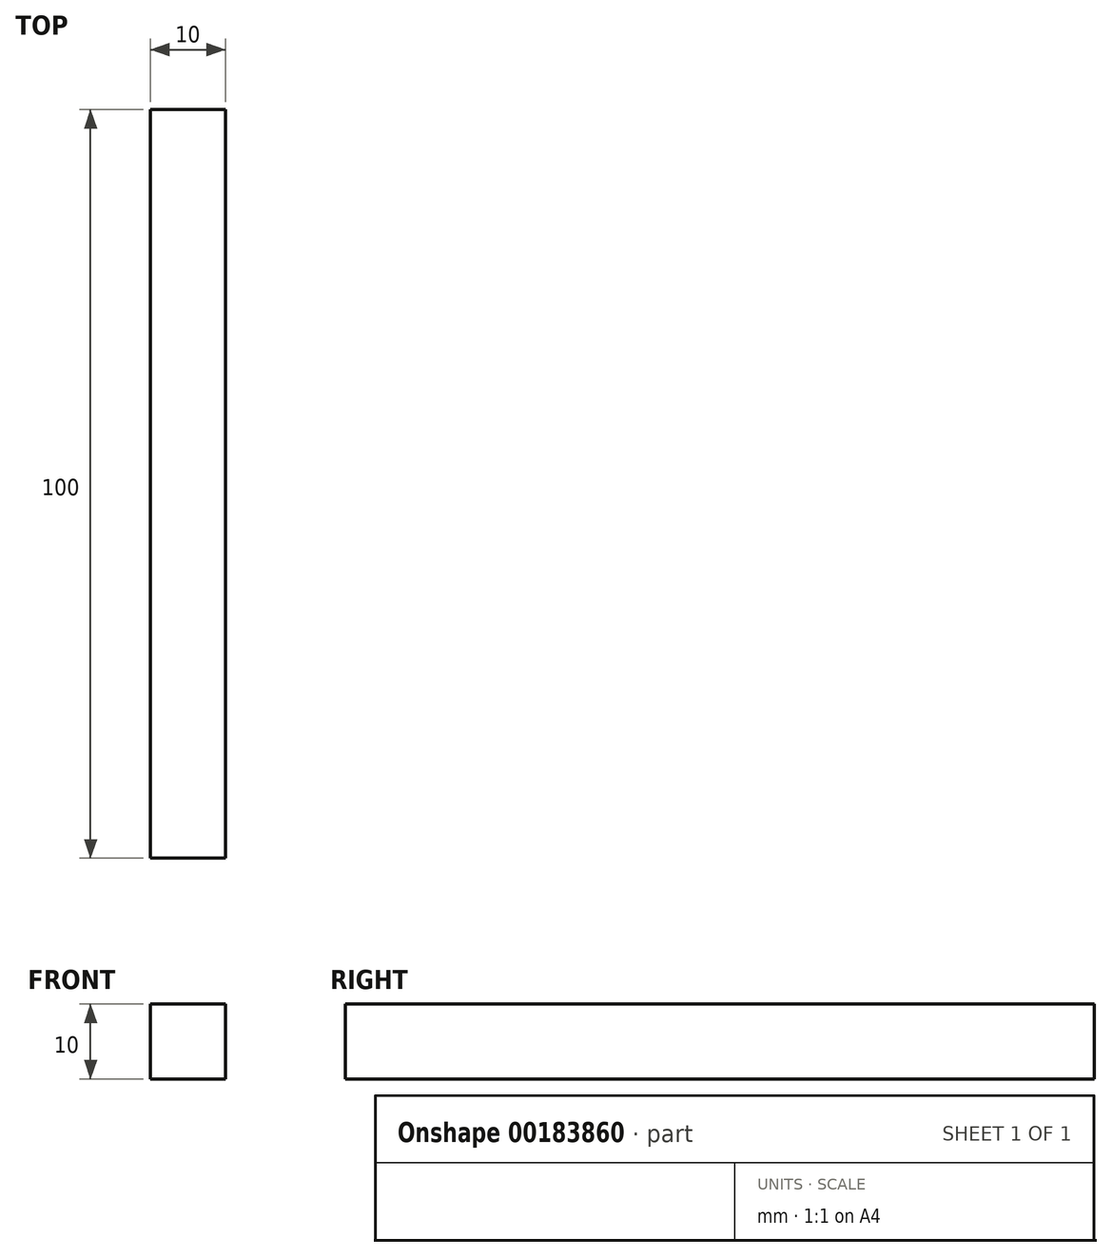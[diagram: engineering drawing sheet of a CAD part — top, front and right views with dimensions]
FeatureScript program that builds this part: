
annotation { "Feature Type Name" : "Feature", "Feature Type Description" : "" }
export const myFeature = defineFeature(function(context is Context, id is Id, definition is map)
    precondition{}
    {
        {
            var Q0;
            Q0=qCreatedBy(makeId("Top.planeOp"),FACE);
            var sketch = newSketch(context, id + "F0", { "sketchPlane" : qUnion([Q0])});
            skLineSegment(sketch, "E0.bottom", {"start": v(5, 50) * mm, "end": v(-5, 50) * mm});
            skLineSegment(sketch, "E0.top", {"start": v(5, -50) * mm, "end": v(-5, -50) * mm});
            skLineSegment(sketch, "E0.left", {"start": v(5, 50) * mm, "end": v(5, -50) * mm});
            skLineSegment(sketch, "E0.right", {"start": v(-5, 50) * mm, "end": v(-5, -50) * mm});
            skPoint(sketch, "E0.middle", {"position": v(0, 0) * mm});
            skSolve(sketch);
        }
        {
            var Q0;
            Q0=makeQuery(id+"F0.imprint","IMPRINT",FACE,{"disambiguationData":[TD([[makeQuery(id+"F0.imprint","IMPRINT",EDGE,{"derivedFrom":sQuery(id+"F0.wireOp",EDGE,"E0.bottom")}),1.0]])]});
            extrude(context, id + "F1", {"entities" : qUnion([Q0]), "depth" : 10 * mm});
        }
    });
